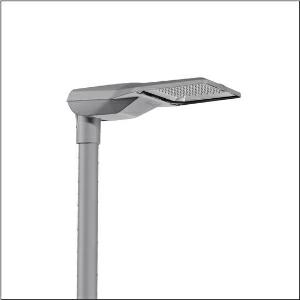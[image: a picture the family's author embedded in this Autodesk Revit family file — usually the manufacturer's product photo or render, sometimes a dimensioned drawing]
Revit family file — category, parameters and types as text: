
# Revit family: streetlight_sl_21_iq_midi___stw1_0a_5xe3e31g08mb_59a2
name_source: partatom
category: Lighting Fixtures
units: mm (PartAtom-declared; Revit-internal decimal feet)

## family parameters
Cut with Voids When Loaded = No
Host = Face
Light Source = No
Part Type = Normal
Room Calculation Point = No
Round Connector Dimension = Use Diameter
Shared = No

## types (1)
- --- (1 x LED, 19500 lm, 146.7 W, 3000K)
    Apparent Load = 147 VA
    CIE Flux Codes = 38 75 98 100 100
    Color Rendering = 70
    Color Temperature = 3000K
    Default Elevation = 1800 mm
    Description = Streetlight SL 21 iQ midi, mast luminaire, primary light control with lens, of PMMA, primary optical cover: cover, of toughened safety glass, transparent, light distribution: STW1.0a, light emission: direct distribution, primary light characteristic: asymmetric, installation type: post-top, side-entry, LED, High Power LED, rated luminous flux: 19.500lm, luminous efficacy: 133lm/W, light colour: 730, colour temperature: 3000K, control: Street-Remote, Auto-Match, Temp-Guard, Lumen-Switch, Night-Set, Smart-Wire, Light-Fading, Desk-Remote (wireless, voltage-free reading and setting of iQ features in the workshop via application-optimized NFC function/RFID function), optimised constant luminous flux control (CLO 2.0), presetting dimming linear, mains connection: 230..240V, AC, 50/60Hz, start of lifetime: 147W, end of service life: 161W, reduction: 62W, luminaire housing, of diecast aluminium, powder-coated, Siteco® metallic grey (DB 702S), corrosivity category C5 mid according to DIN EN ISO 12944, please order mast flange separately, inclination adjustable: 0°, 5°, 10°, 15°, sealing non-destructively replaceable, multi-level sealing system, length: 644mm, width: 335mm, height: 110mm, mast flange for spigot size: 42mm (side-entry): 5XC10008XM4, 60/48mm (side-entry/post-top): 5XC10108XM2, 76/60mm (side-entry/post-top): 5XC10108XM1, protection rating (complete): IP66, insulation class (complete): insulation class II (safety insulation), certification: CE, ENEC, ENEC+, VDE, impact resistance: IK09, permissible operating ambient temperature for outdoor applications: -40..+50°C, standard-compliant lighting for roads and squares, packaging unit: 1 piece

Light Distribution: STW1.0a
    Height = 111 mm
    Lamp = 1 x LED
    Lamp Light Flux = 19500 lm
    Lamp Power = 146.7 W
    Lamp count = 1
    Length = 644 mm
    Luminous efficacy = 133 lm/W
    Manufacturer = Siteco
    ModVariant = No
    Model = 5XE3E31G08MB
    Number of Poles = 1
    OnlyDefault = Yes
    Power Factor = 1
    Product Name = Streetlight SL 21 iQ midi | STW1.0a
    Product group = mast luminaire | pylon top
    ProductGroupID = 6100
    Protection Class = Protection class II
    Protection Degree = IP 66
    RLX_Detail_Level = 1
    RLX_Emergency_Light_Flux = 0 lm
    RLX_Emergency_Type = 0
    RLX_Emergency_Type_DB = No
    RlxData = <blob elided: 90537 chars, md5=a2a23cc2>
    Socket = socket
    Standby Power = 0 W
    System Light Flux = 19499 lm
    System Power = 147 W
    Type Comments = factory setting: luminous flux: 100 % | dim-lin: 254 | 753 mA
    Type Image = l_1004298.jpg
    URL = http://relux.com
    VarID = @adj_121825
    Voltage = 0 V
    Weight = 0.00 kg
    Width = 336 mm

## geometry (parser evidence)
native form markers: Blend x4, Sweep x11
no freeform markers — native parametric forms only
